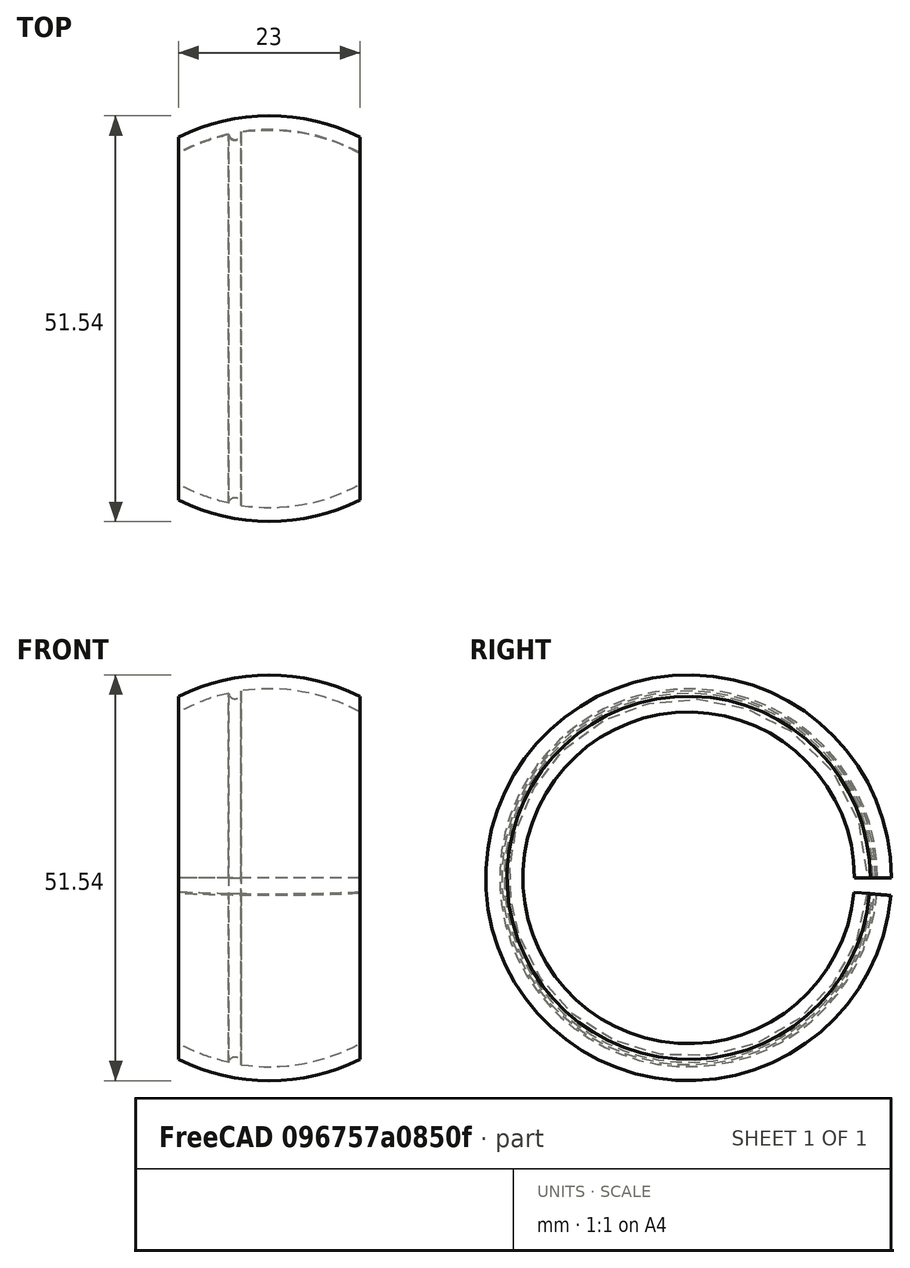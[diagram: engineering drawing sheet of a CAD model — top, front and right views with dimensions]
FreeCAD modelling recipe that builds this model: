
FCSTD DOCUMENT  (FreeCAD 0.18R16110 (Git))
Label: bearinghubbaguehandle
License: All rights reserved
LicenseURL: http://en.wikipedia.org/wiki/All_rights_reserved
objects: Mesh::Feature×2, Sketcher::SketchObject×1, Part::Revolution×1
note: 2 computed .brp shape members not serialized (recipe doc carries the construction recipe); baked Part::Feature solids carry a one-line shape summary decoded from their .brp

FEATURE [Sketcher::SketchObject] Sketch
  sketch-geometry (9):
    g0: ArcOfCircle CenterX=0 CenterY=0 CenterZ=0 NormalX=0 NormalY=0 NormalZ=1 AngleXU=0 Radius=24 StartAngle=1.07109 EndAngle=1.72066
    g1: ArcOfCircle CenterX=0 CenterY=0 CenterZ=0 NormalX=0 NormalY=0 NormalZ=1 AngleXU=0 Radius=25.7733 StartAngle=1.10828 EndAngle=2.03331
    g2: LineSegment StartX=11.5 StartY=23.0654 StartZ=0 EndX=11.5 EndY=21.0654 EndZ=0
    g3: LineSegment StartX=-11.5 StartY=23.0654 StartZ=0 EndX=-11.5 EndY=21.0654 EndZ=0
    g4: LineSegment [constr] StartX=-11.5 StartY=21.0654 StartZ=0 EndX=11.5 EndY=21.0654 EndZ=0
    g5: GeomPoint X=-7.36571 Y=22.8418 Z=0
    g6: GeomPoint X=-7.3108 Y=22.8515 Z=0
    g7: ArcOfCircle CenterX=-4.35815 CenterY=23.5321 CenterZ=0 NormalX=0 NormalY=0 NormalZ=1 AngleXU=0 Radius=0.8 StartAngle=3.25663 EndAngle=6.53441
    g8: ArcOfCircle CenterX=-5.45555e-05 CenterY=3.76995e-05 CenterZ=0 NormalX=0 NormalY=0 NormalZ=1 AngleXU=0 Radius=23.9999 StartAngle=1.78718 EndAngle=2.0705
  constraints (18):
    c: Coincident(g0,g-1)
    c: Coincident(g1,g0)
    c: Coincident(g2,g1)
    c: Coincident(g2,g0)
    c: Vertical(g2)
    c: Coincident(g3,g1)
    c: Coincident(g3,g8)
    c: Vertical(g3)
    c: Symmetric(g0,g8,g-2)
    c: DistanceY(g2,g2) = 2
    c: Coincident(g4,g8)
    c: Coincident(g4,g0)
    c: Radius(g0) = 24
    c: DistanceX(g4,g4) = 23
    c: PointOnObject(g5,g0)
    c: Radius(g7) = 0.8
    c: Coincident(g7,g0)
    c: Coincident(g8,g7)
FEATURE [Part::Revolution] Revolve
  Angle = 355
  Axis = (1,0,0)
  Base = (0,0,0)
  FaceMakerClass = Part::FaceMakerBullseye
  Solid = true
  Source = -> Sketch
  Symmetric = false
FEATURE [Mesh::Feature] handle
  Placement = pos=(6,26.4,-2.2) rot=(0,1,0;1.5708rad)
FEATURE [Mesh::Feature] handle001
  Placement = pos=(6,26.4,2) rot=(0,1,0;1.5708rad)
